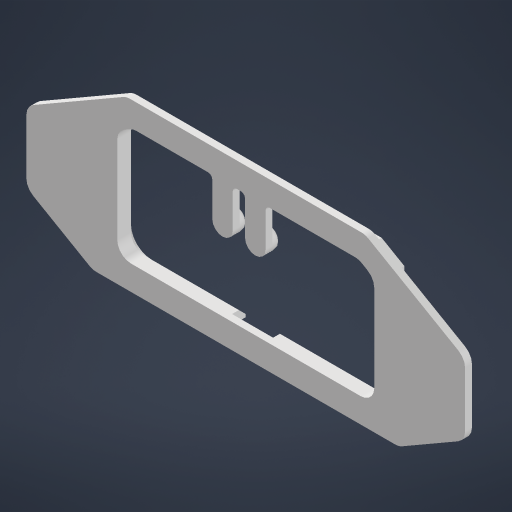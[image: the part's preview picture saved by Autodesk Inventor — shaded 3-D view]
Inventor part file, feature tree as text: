
AUTODESK INVENTOR PART (.ipt)
format: ipt  version: 2023.4 (Build 274418000, 418)  size: 346,624 bytes
history: native  units: mm
features: other x4, extrude x3, sketch x2, fillet x2, plane x1, chamfer x1, reference x1, projected_geometry x1
ambient origin geometry x8: Origin, YZ Plane, XZ Plane, XY Plane, X Axis, Y Axis, Z Axis, Center Point
bodies: Solid1 (feature_tree)
feature tree (15):
  plane  "Work Plane1"
  extrude  "Extrusion1"  Depth=1.25mm TaperAngle=0.0deg
  sketch  "Sketch2"  dims[d12=1.25mm d13=2.0mm d14=45.0deg d15=0.25mm d16=2.0mm d17=2.5mm d18=1.75mm d19=0.25mm d20=2.5mm d21=14.0mm d22=14.0mm d23=2.5mm d30=3.0mm d31=6.0mm d32=3.75mm d33=3.75mm d34=1.5mm d35=0.0mm d36=0.75mm d37=7.0mm d38=1.25mm d29=0.5mm d39=0.5mm d40=0.872665mm d41=0.5mm d42=0.872665mm]
  extrude  "Extrusion2"  Depth=1.25mm
  extrude  "Extrusion3"  Depth=1.25mm
  fillet  "Fillet1"  Radius=2.5mm
  chamfer  "Chamfer1"  Distance=1.75mm
  fillet  "Fillet2"  Radius=0.25mm
  sketch  "Sketch1"  dims[d1=2.5mm d2=0.0mm d6=1.25mm d7=0.0mm]
  reference  "Reference1"
  projected_geometry  "Projected Loop2"
  parser-record x1  (decoder bookkeeping rows leaked as tree rows — omitted from the tree; the rows remain in map.json)
  other  "Joystick Enclosure.iam"
  other  "Joystick Bottom:1"
  other  "Assembly1"
note: 1 file-system path scrubbed to <path> (originals preserved in map.json)
